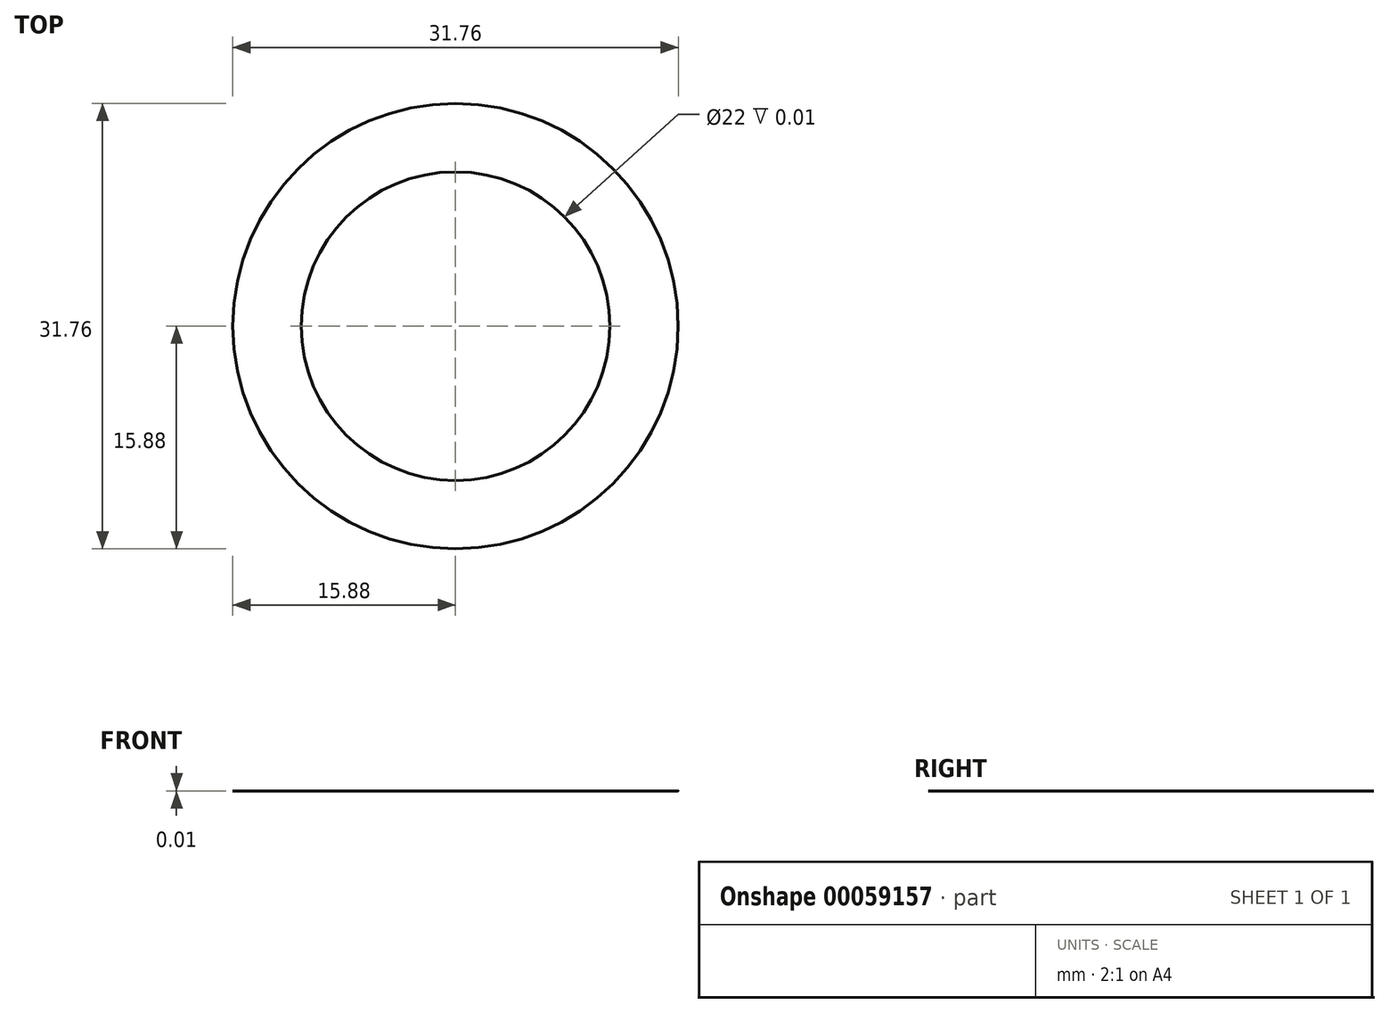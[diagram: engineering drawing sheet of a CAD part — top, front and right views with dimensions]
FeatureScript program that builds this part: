
annotation { "Feature Type Name" : "Feature", "Feature Type Description" : "" }
export const myFeature = defineFeature(function(context is Context, id is Id, definition is map)
    precondition{}
    {
        {
            var Q0;
            Q0=qCreatedBy(makeId("Top.planeOp"),FACE);
            var sketch = newSketch(context, id + "F0", { "sketchPlane" : qUnion([Q0])});
            skCircle(sketch, "E0", {"center": v(0, 0) * mm, "radius": 15.87 * mm});
            skCircle(sketch, "E1", {"center": v(0, 0) * mm, "radius": 11 * mm});
            skSolve(sketch);
        }
        {
            var Q0;
            Q0=makeQuery(id+"F0.imprint","IMPRINT",FACE,{"disambiguationData":[TD([[makeQuery(id+"F0.imprint","IMPRINT",EDGE,{"derivedFrom":sQuery(id+"F0.wireOp",EDGE,"E0")}),1.0]])]});
            var Q1;
            Q1=sQuery(id+"F0.wireOp",EDGE,"E0");
            extrude(context, id + "F1", {"entities" : qUnion([Q0]), "surfaceEntities" : qUnion([Q1]), "depth" : 1 / 101.6 * mm});
        }
        {
            var Q0;
            Q0=qCreatedBy(makeId("Front.planeOp"),FACE);
            var sketch = newSketch(context, id + "F2", { "sketchPlane" : qUnion([Q0])});
            skLineSegment(sketch, "E2", {"start": v(15.87, 2.74) * mm, "end": v(15.87, 0.43) * mm});
            skLineSegment(sketch, "E3", {"start": v(15.88, 0.43) * mm, "end": v(13.88, 1.59) * mm});
            skLineSegment(sketch, "E4", {"start": v(13.88, 1.59) * mm, "end": v(15.88, 2.74) * mm});
            skLineSegment(sketch, "E5", {"start": v(0, 0) * mm, "end": v(0, 19.15) * mm, "construction": true});
            skLineSegment(sketch, "E6.1.0.0", {"start": v(13.88, 4.76) * mm, "end": v(15.88, 5.92) * mm});
            skLineSegment(sketch, "E6.1.0.1", {"start": v(15.88, 3.6) * mm, "end": v(13.88, 4.76) * mm});
            skLineSegment(sketch, "E6.1.0.2", {"start": v(15.88, 5.92) * mm, "end": v(15.88, 3.6) * mm});
            skLineSegment(sketch, "E6.direction1", {"start": v(15.88, 2.74) * mm, "end": v(15.88, 5.92) * mm, "construction": true});
            skLineSegment(sketch, "E7", {"start": v(13.88, 1.59) * mm, "end": v(13.88, 4.76) * mm, "construction": true});
            skPoint(sketch, "E8", {"position": v(13.88, 3.18) * mm});
            skSolve(sketch);
        }
        {
            var Q0;
            Q0 = qSketchRegion(id + "F2", true);
            var Q1;
            Q1=sQuery(id+"F2.wireOp",EDGE,"E5");
            revolve(context, id + "F3", {"operationType" : NewBodyOperationType.REMOVE, "entities" : qUnion([Q0]), "axis" : qUnion([Q1]), "revolveType" : RevolveType.FULL, "oppositeDirection" : true});
        }
    });
